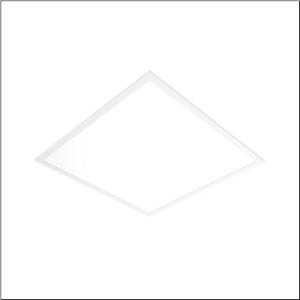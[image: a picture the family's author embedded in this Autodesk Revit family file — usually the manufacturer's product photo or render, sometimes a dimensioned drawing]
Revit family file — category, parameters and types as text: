
# Revit family: apollon_r__41_51mh11w72443_9aaa
name_source: partatom
category: Lighting Fixtures
units: mm (PartAtom-declared; Revit-internal decimal feet)

## family parameters
Cut with Voids When Loaded = No
Host = Face
Light Source = No
Part Type = Normal
Room Calculation Point = No
Round Connector Dimension = Use Diameter
Shared = No

## types (1)
- Apollon® 41 (1 x LED, 3700 lm, 28.5 W, 4000K)
    Apparent Load = 29 VA
    CIE Flux Codes = 61 87 97 100 100
    Color Rendering = 80
    Color Temperature = 4000K
    Default Elevation = 1800 mm
    Description = Apollon® 41, office luminaire, primary optical cover: prismatic diffuser, of PS, light emission: direct distribution, primary light characteristic: symmetric, installation type: lay-in mounting, LED, rated luminous flux: 3.700lm, luminous efficacy: 130lm/W, light colour: 840, colour temperature: 4000K, with terminal, 3-pole, mains connection: 220..240V, AC, 50/60Hz, housing, of aluminium section, traffic white (RAL 9016), module: M625, length: 620mm, width: 620mm, height: 40mm, housing upper side, of sheet steel, protection rating (complete): IP20, protection rating (lamp compartment, on room side): IP40, insulation class (complete): insulation class II (safety insulation), certification: CE, ENEC, permissible operating ambient temperature: -20..+40°C, packaging unit: 1 piece
    Height = 0 mm  [stored 0 ft]
    Lamp = 1 x LED
    Lamp Light Flux = 3700 lm
    Lamp Power = 28.5 W
    Lamp count = 1
    Length = 620 mm
    Luminous efficacy = 130 lm/W
    Manufacturer = Siteco
    ModVariant = No
    Model = 51MH11W72443
    Mounting Place = Ceiling
    Mounting Type = Recessed
    Number of Poles = 1
    OnlyDefault = Yes
    Power Factor = 1
    Product Name = Apollon® 41
    Product group = office luminaire | ceiling recessed
    ProductGroupID = 401
    Protection Class = Protection class II
    Protection Degree = IP 20
    RLX_Detail_Level = 1
    RLX_Emergency_Light_Flux = 0 lm
    RLX_Emergency_Type = 0
    RLX_Emergency_Type_DB = No
    RlxData = <blob elided: 12181 chars, md5=730ccbda>
    Socket = socket
    Standby Power = 0 W
    System Light Flux = 3700 lm
    System Power = 29 W
    Type Comments = Product without accessories
    Type Image = l_1291024.jpg
    URL = http://relux.com
    VarID = ---
    Voltage = 0 V
    Weight = 0.00 kg
    Width = 620 mm

note: [stored X ft] marks values corroborated as IEEE doubles in the binary element streams (Revit-internal decimal feet)

## geometry (parser evidence)
native form markers: Sweep x11
no freeform markers — native parametric forms only
